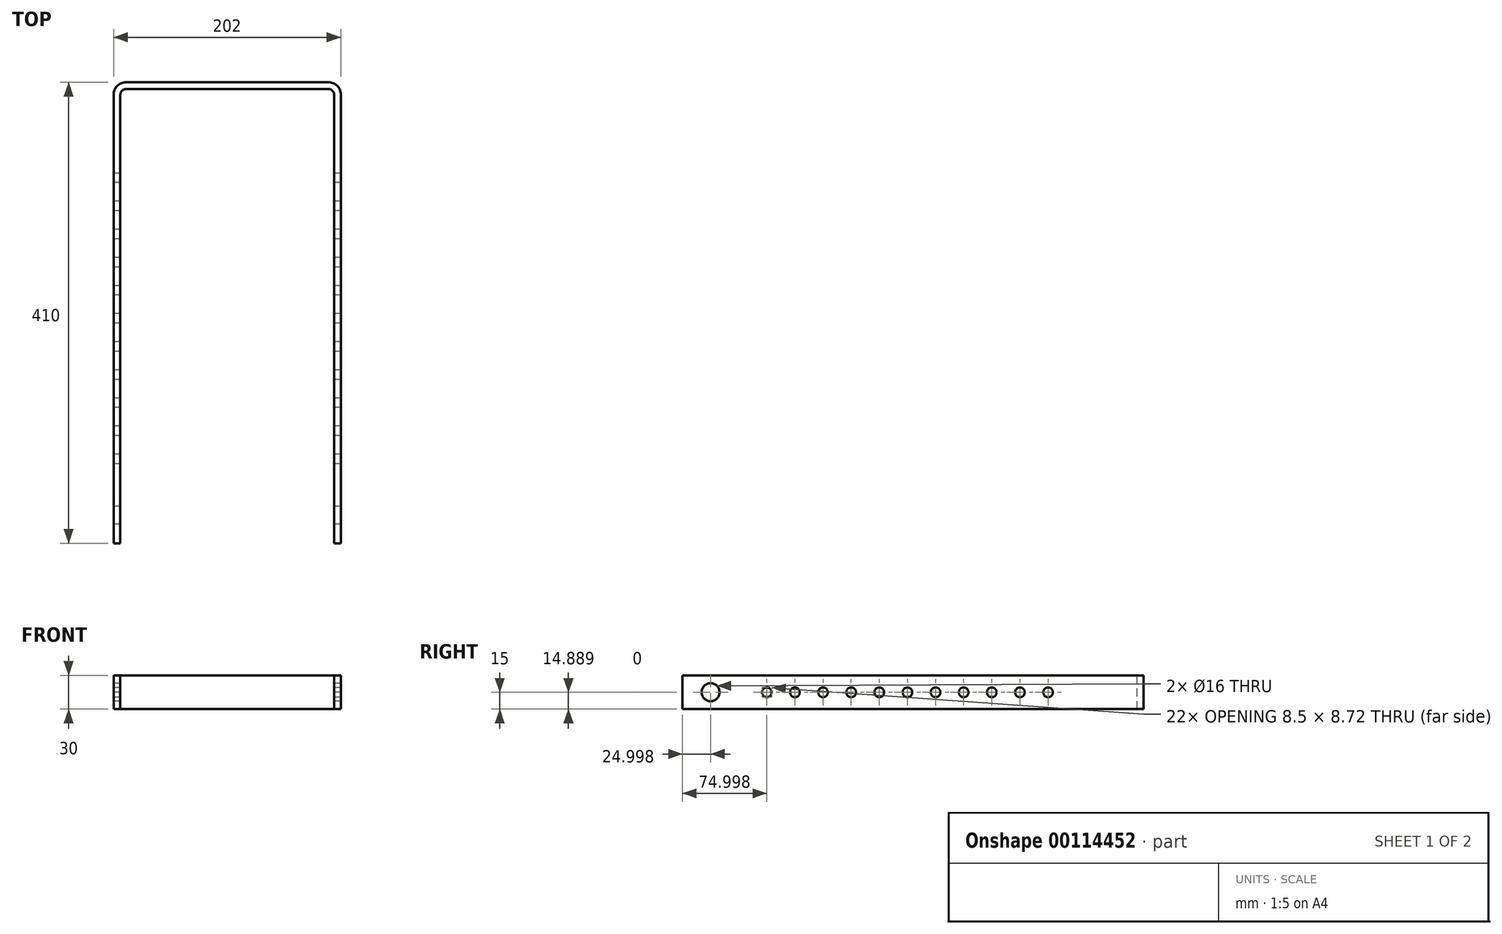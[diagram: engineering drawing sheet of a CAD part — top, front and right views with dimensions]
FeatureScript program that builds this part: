
annotation { "Feature Type Name" : "Feature", "Feature Type Description" : "" }
export const myFeature = defineFeature(function(context is Context, id is Id, definition is map)
    precondition{}
    {
        {
            var Q0;
            Q0=qCreatedBy(makeId("Top.planeOp"),FACE);
            var sketch = newSketch(context, id + "F0", { "sketchPlane" : qUnion([Q0])});
            skLineSegment(sketch, "E0", {"start": v(-101, -22.5) * mm, "end": v(-101, 376.5) * mm});
            skLineSegment(sketch, "E1", {"start": v(-90, 387.5) * mm, "end": v(0, 387.5) * mm});
            skLineSegment(sketch, "E2.0", {"start": v(-90, 381.5) * mm, "end": v(0, 381.5) * mm});
            skLineSegment(sketch, "E2.1", {"start": v(-95, -22.5) * mm, "end": v(-95, 376.5) * mm});
            skLineSegment(sketch, "E3", {"start": v(-101, -22.5) * mm, "end": v(-95, -22.5) * mm});
            skLineSegment(sketch, "E4.MirrorCS", {"start": v(95, -22.5) * mm, "end": v(95, 376.5) * mm});
            skLineSegment(sketch, "E5.MirrorCS", {"start": v(101, -22.5) * mm, "end": v(95, -22.5) * mm});
            skLineSegment(sketch, "E6.MirrorCS", {"start": v(101, -22.5) * mm, "end": v(101, 376.5) * mm});
            skLineSegment(sketch, "E7.MirrorCS", {"start": v(90, 387.5) * mm, "end": v(0, 387.5) * mm});
            skLineSegment(sketch, "E8.MirrorCS", {"start": v(90, 381.5) * mm, "end": v(0, 381.5) * mm});
            skPoint(sketch, "E9.visualSharp", {"position": v(-95, 381.5) * mm});
            skArc(sketch, "E9.filletArc", {"start": v(-90, 381.5) * mm, "mid": v(-93.54, 380.03) * mm, "end": v(-95, 376.5) * mm});
            skPoint(sketch, "E10.visualSharp", {"position": v(-101, 387.5) * mm});
            skArc(sketch, "E10.filletArc", {"start": v(-90, 387.5) * mm, "mid": v(-97.78, 384.28) * mm, "end": v(-101, 376.5) * mm});
            skPoint(sketch, "E11.visualSharp", {"position": v(101, 387.5) * mm});
            skArc(sketch, "E11.filletArc", {"start": v(101, 376.5) * mm, "mid": v(97.78, 384.28) * mm, "end": v(90, 387.5) * mm});
            skPoint(sketch, "E12.visualSharp", {"position": v(95, 381.5) * mm});
            skArc(sketch, "E12.filletArc", {"start": v(95, 376.5) * mm, "mid": v(93.54, 380.03) * mm, "end": v(90, 381.5) * mm});
            skSolve(sketch);
        }
        {
            var Q0;
            Q0 = qSketchRegion(id + "F0", true);
            extrude(context, id + "F1", {"entities" : qUnion([Q0]), "depth" : 30 * mm});
        }
        {
            var Q0;
            Q0=makeQuery(id+"F1.opExtrude","SWEPT_FACE",FACE,{"disambiguationData":[OSD([sQuery(id+"F0.wireOp",EDGE,"E0")])]});
            var sketch = newSketch(context, id + "F2", { "sketchPlane" : qUnion([Q0])});
            skCircle(sketch, "E13", {"center": v(-2.5, 15) * mm, "radius": 8 * mm});
            skPoint(sketch, "E13.centerSnap0", {"position": v(22.5, 15) * mm});
            skCircle(sketch, "E14", {"center": v(-52.5, 15) * mm, "radius": 4.25 * mm});
            skCircle(sketch, "E15.0.1.0", {"center": v(-52.5, 14.78) * mm, "radius": 4.25 * mm});
            skCircle(sketch, "E15.1.0.0", {"center": v(-77.5, 15) * mm, "radius": 4.25 * mm});
            skCircle(sketch, "E15.1.1.0", {"center": v(-77.5, 14.78) * mm, "radius": 4.25 * mm});
            skCircle(sketch, "E15.2.0.0", {"center": v(-102.5, 15) * mm, "radius": 4.25 * mm});
            skCircle(sketch, "E15.2.1.0", {"center": v(-102.5, 14.78) * mm, "radius": 4.25 * mm});
            skCircle(sketch, "E15.3.0.0", {"center": v(-127.5, 15) * mm, "radius": 4.25 * mm});
            skCircle(sketch, "E15.3.1.0", {"center": v(-127.5, 14.78) * mm, "radius": 4.25 * mm});
            skCircle(sketch, "E15.4.0.0", {"center": v(-152.5, 15) * mm, "radius": 4.25 * mm});
            skCircle(sketch, "E15.4.1.0", {"center": v(-152.5, 14.78) * mm, "radius": 4.25 * mm});
            skCircle(sketch, "E15.5.0.0", {"center": v(-177.5, 15) * mm, "radius": 4.25 * mm});
            skCircle(sketch, "E15.5.1.0", {"center": v(-177.5, 14.78) * mm, "radius": 4.25 * mm});
            skCircle(sketch, "E15.6.0.0", {"center": v(-202.5, 15) * mm, "radius": 4.25 * mm});
            skCircle(sketch, "E15.6.1.0", {"center": v(-202.5, 14.78) * mm, "radius": 4.25 * mm});
            skCircle(sketch, "E15.7.0.0", {"center": v(-227.5, 15) * mm, "radius": 4.25 * mm});
            skCircle(sketch, "E15.7.1.0", {"center": v(-227.5, 14.78) * mm, "radius": 4.25 * mm});
            skCircle(sketch, "E15.8.0.0", {"center": v(-252.5, 15) * mm, "radius": 4.25 * mm});
            skCircle(sketch, "E15.8.1.0", {"center": v(-252.5, 14.78) * mm, "radius": 4.25 * mm});
            skCircle(sketch, "E15.9.0.0", {"center": v(-277.5, 15) * mm, "radius": 4.25 * mm});
            skCircle(sketch, "E15.9.1.0", {"center": v(-277.5, 14.78) * mm, "radius": 4.25 * mm});
            skCircle(sketch, "E15.10.0.0", {"center": v(-302.5, 15) * mm, "radius": 4.25 * mm});
            skCircle(sketch, "E15.10.1.0", {"center": v(-302.5, 14.78) * mm, "radius": 4.25 * mm});
            skLineSegment(sketch, "E15.direction1", {"start": v(0, 0) * mm, "end": v(-25, 0) * mm, "construction": true});
            skLineSegment(sketch, "E15.direction2", {"start": v(0, 0) * mm, "end": v(0, -0.22) * mm, "construction": true});
            skSolve(sketch);
        }
        {
            var Q0;
            Q0 = qSketchRegion(id + "F2", true);
            extrude(context, id + "F3", {"entities" : qUnion([Q0]), "operationType" : NewBodyOperationType.REMOVE, "endBound" : BoundingType.THROUGH_ALL, "oppositeDirection" : true, "depth" : 25 * mm});
        }
    });
